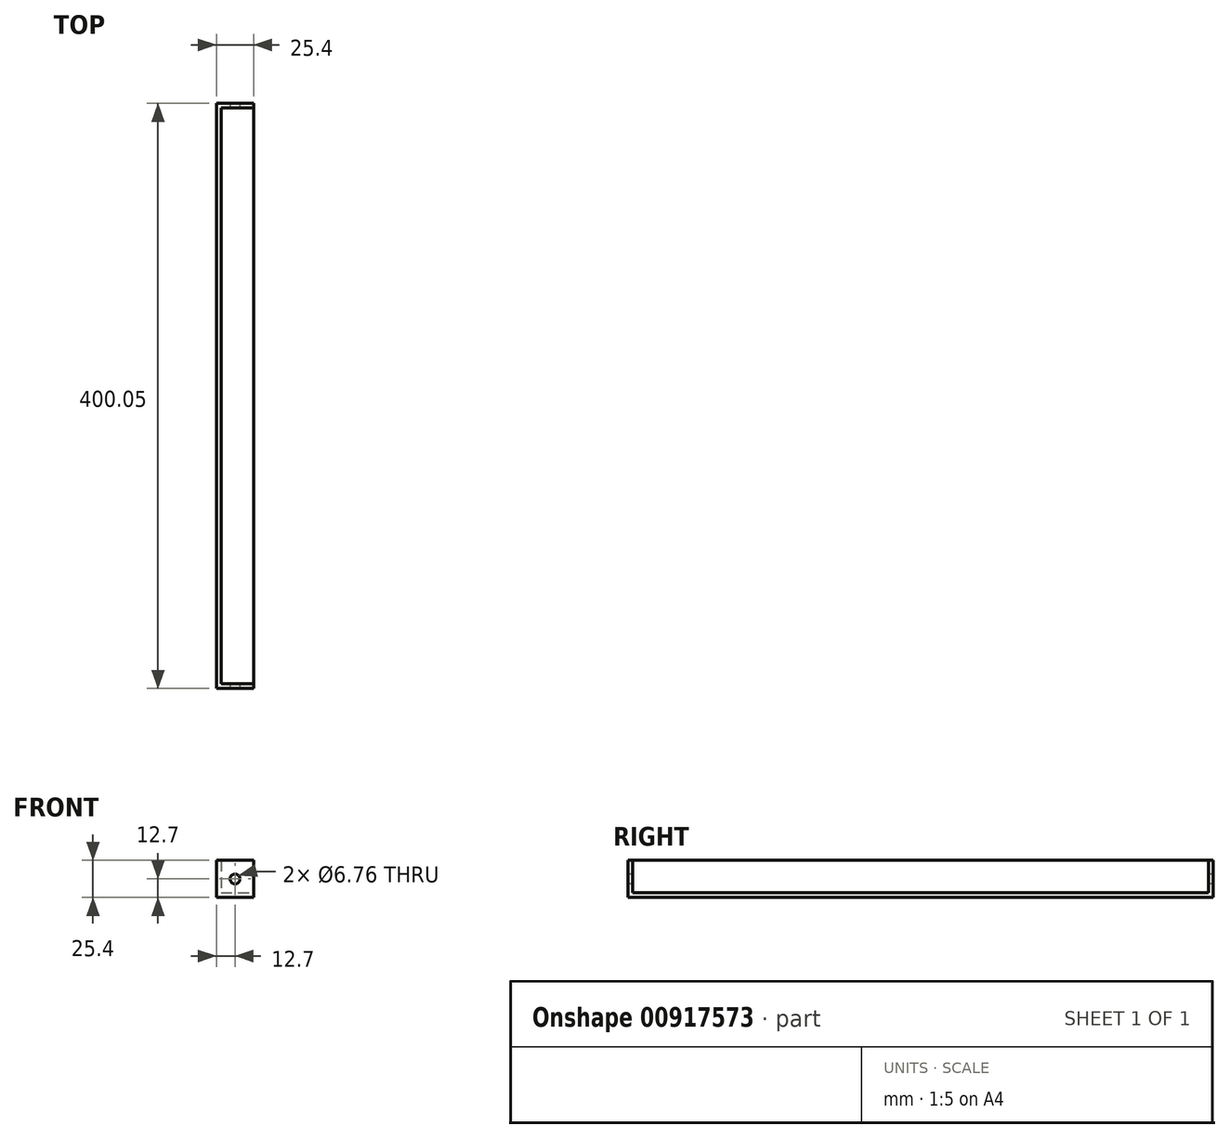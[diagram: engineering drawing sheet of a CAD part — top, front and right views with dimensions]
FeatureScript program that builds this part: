
annotation { "Feature Type Name" : "Feature", "Feature Type Description" : "" }
export const myFeature = defineFeature(function(context is Context, id is Id, definition is map)
    precondition{}
    {
        {
            var Q0;
            Q0=qCreatedBy(makeId("Front.planeOp"),FACE);
            var sketch = newSketch(context, id + "F0", { "sketchPlane" : qUnion([Q0])});
            skLineSegment(sketch, "E0", {"start": v(0, 0) * mm, "end": v(0, 25.4) * mm});
            skLineSegment(sketch, "E1", {"start": v(0, 25.4) * mm, "end": v(3.17, 25.4) * mm});
            skLineSegment(sketch, "E2", {"start": v(3.17, 25.4) * mm, "end": v(3.18, 3.17) * mm});
            skLineSegment(sketch, "E3", {"start": v(3.18, 3.17) * mm, "end": v(25.4, 3.18) * mm});
            skLineSegment(sketch, "E4", {"start": v(25.4, 3.18) * mm, "end": v(25.4, 0) * mm});
            skLineSegment(sketch, "E5", {"start": v(25.4, 0) * mm, "end": v(0, 0) * mm});
            skSolve(sketch);
        }
        {
            var Q0;
            Q0=makeQuery(id+"F0.imprint","IMPRINT",FACE,{"disambiguationData":[TD([[makeQuery(id+"F0.imprint","IMPRINT",EDGE,{"derivedFrom":sQuery(id+"F0.wireOp",EDGE,"E0")}),-1.0]])]});
            extrude(context, id + "F1", {"entities" : qUnion([Q0]), "depth" : 400.05 * mm, "offsetDistance" : 25.4 * mm});
        }
        {
            var Q0;
            Q0=makeQuery(id+"F1.opExtrude","CAP_FACE",FACE,{"disambiguationData":[OSD([sQuery(id+"F0.wireOp",EDGE,"E0"),sQuery(id+"F0.wireOp",EDGE,"E1"),sQuery(id+"F0.wireOp",EDGE,"E2"),sQuery(id+"F0.wireOp",EDGE,"E3"),sQuery(id+"F0.wireOp",EDGE,"E4"),sQuery(id+"F0.wireOp",EDGE,"E5")])],"isStart":false});
            var sketch = newSketch(context, id + "F2", { "sketchPlane" : qUnion([Q0])});
            skLineSegment(sketch, "E6.bottom", {"start": v(3.18, 3.17) * mm, "end": v(25.4, 3.17) * mm});
            skLineSegment(sketch, "E6.top", {"start": v(3.17, 25.4) * mm, "end": v(25.4, 25.4) * mm});
            skLineSegment(sketch, "E6.left", {"start": v(3.18, 3.17) * mm, "end": v(3.18, 25.4) * mm});
            skLineSegment(sketch, "E6.right", {"start": v(25.4, 3.17) * mm, "end": v(25.4, 25.4) * mm});
            skSolve(sketch);
        }
        {
            var Q0;
            Q0=makeQuery(id+"F2.imprint","IMPRINT",FACE,{"disambiguationData":[TD([[makeQuery(id+"F2.imprint","IMPRINT",EDGE,{"derivedFrom":sQuery(id+"F2.wireOp",EDGE,"E6.bottom")}),1.0]])]});
            extrude(context, id + "F3", {"entities" : qUnion([Q0]), "operationType" : NewBodyOperationType.ADD, "oppositeDirection" : true, "depth" : 3.17 * mm, "offsetDistance" : 25.4 * mm});
        }
        {
            var Q0;
            Q0=makeQuery(id+"F1.opExtrude","CAP_FACE",FACE,{"disambiguationData":[OSD([sQuery(id+"F0.wireOp",EDGE,"E0"),sQuery(id+"F0.wireOp",EDGE,"E1"),sQuery(id+"F0.wireOp",EDGE,"E2"),sQuery(id+"F0.wireOp",EDGE,"E3"),sQuery(id+"F0.wireOp",EDGE,"E4"),sQuery(id+"F0.wireOp",EDGE,"E5")])],"isStart":true});
            var sketch = newSketch(context, id + "F4", { "sketchPlane" : qUnion([Q0])});
            skLineSegment(sketch, "E7.bottom", {"start": v(-3.18, 3.17) * mm, "end": v(-25.4, 3.17) * mm});
            skLineSegment(sketch, "E7.top", {"start": v(-3.18, 25.4) * mm, "end": v(-25.4, 25.4) * mm});
            skLineSegment(sketch, "E7.left", {"start": v(-3.18, 3.17) * mm, "end": v(-3.18, 25.4) * mm});
            skLineSegment(sketch, "E7.right", {"start": v(-25.4, 3.17) * mm, "end": v(-25.4, 25.4) * mm});
            skSolve(sketch);
        }
        {
            var Q0;
            Q0=makeQuery(id+"F4.imprint","IMPRINT",FACE,{"disambiguationData":[TD([[makeQuery(id+"F4.imprint","IMPRINT",EDGE,{"derivedFrom":sQuery(id+"F4.wireOp",EDGE,"E7.bottom")}),-1.0]])]});
            extrude(context, id + "F5", {"entities" : qUnion([Q0]), "operationType" : NewBodyOperationType.ADD, "oppositeDirection" : true, "depth" : 3.17 * mm, "offsetDistance" : 25.4 * mm});
        }
        {
            var Q0;
            Q0=makeQuery(id+"F3.boolean.opBoolean","MERGE",FACE,{"derivedFrom":[makeQuery(id+"F1.opExtrude","CAP_FACE",FACE,{"disambiguationData":[OSD([sQuery(id+"F0.wireOp",EDGE,"E0"),sQuery(id+"F0.wireOp",EDGE,"E1"),sQuery(id+"F0.wireOp",EDGE,"E2"),sQuery(id+"F0.wireOp",EDGE,"E3"),sQuery(id+"F0.wireOp",EDGE,"E4"),sQuery(id+"F0.wireOp",EDGE,"E5")])],"isStart":false}),makeQuery(id+"F3.opExtrude","CAP_FACE",FACE,{"disambiguationData":[OSD([sQuery(id+"F2.wireOp",EDGE,"E6.bottom"),sQuery(id+"F2.wireOp",EDGE,"E6.top"),sQuery(id+"F2.wireOp",EDGE,"E6.left"),sQuery(id+"F2.wireOp",EDGE,"E6.right")])],"isStart":true})]});
            var sketch = newSketch(context, id + "F6", { "sketchPlane" : qUnion([Q0])});
            skPoint(sketch, "E8", {"position": v(12.7, 12.7) * mm});
            skPoint(sketch, "E8.positionSnap0", {"position": v(0, 12.7) * mm});
            skSolve(sketch);
        }
        {
            var Q0;
            Q0=sQuery(id+"F6.wireOp",VERTEX,"E8");
            var Q1;
            Q1=makeQuery(id+"F1.opExtrude","SWEPT_BODY",BODY,{"disambiguationData":[OSD([sQuery(id+"F0.wireOp",EDGE,"E0"),sQuery(id+"F0.wireOp",EDGE,"E1"),sQuery(id+"F0.wireOp",EDGE,"E2"),sQuery(id+"F0.wireOp",EDGE,"E3"),sQuery(id+"F0.wireOp",EDGE,"E4"),sQuery(id+"F0.wireOp",EDGE,"E5")])]});
            hole(context, id + "F7", {"style" : HoleStyle.SIMPLE, "endStyle" : HoleEndStyle.THROUGH, "holeDiameter" : 6.76 * mm, "majorDiameter" : 6.35 * mm, "isTappedThrough" : true, "tappedDepth" : 12.7 * mm, "tapClearance" : 3, "locations" : qUnion([Q0]), "scope" : qUnion([Q1])});
        }
    });
